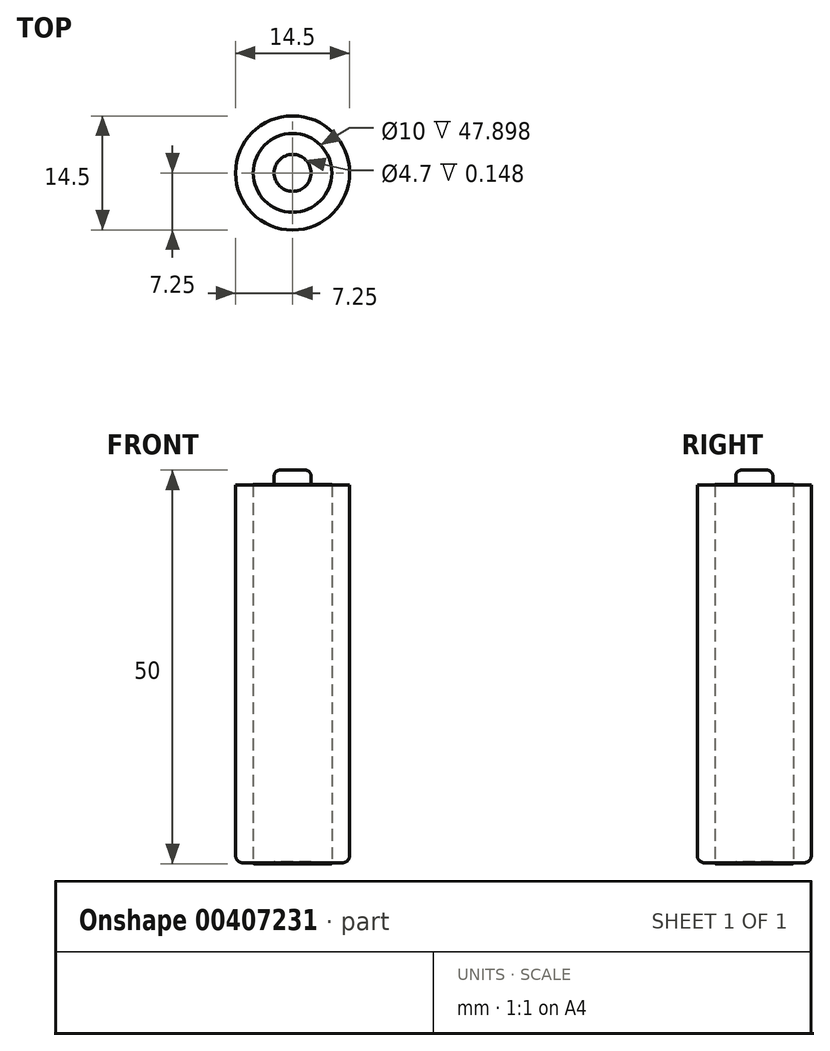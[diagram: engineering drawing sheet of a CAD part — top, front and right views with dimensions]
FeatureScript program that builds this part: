
annotation { "Feature Type Name" : "Feature", "Feature Type Description" : "" }
export const myFeature = defineFeature(function(context is Context, id is Id, definition is map)
    precondition{}
    {
        {
            var Q0;
            Q0=qCreatedBy(makeId("Top.planeOp"),FACE);
            var sketch = newSketch(context, id + "F0", { "sketchPlane" : qUnion([Q0])});
            skCircle(sketch, "E0", {"center": v(0, 0) * mm, "radius": 7.25 * mm});
            skCircle(sketch, "E1", {"center": v(0, 0) * mm, "radius": 2.35 * mm});
            skCircle(sketch, "E2", {"center": v(0, 0) * mm, "radius": 5 * mm});
            skSolve(sketch);
        }
        {
            var Q0;
            Q0=makeQuery(id+"F0.imprint","IMPRINT",FACE,{"disambiguationData":[TD([[makeQuery(id+"F0.imprint","IMPRINT",EDGE,{"derivedFrom":sQuery(id+"F0.wireOp",EDGE,"E1")}),1.0]])]});
            extrude(context, id + "F1", {"entities" : qUnion([Q0]), "depth" : 50 * mm, "offsetDistance" : 25.4 * mm, "hasSecondDirection" : true, "secondDirectionOppositeDirection" : false, "secondDirectionDepth" : 0.25 * mm});
        }
        {
            var Q0;
            Q0=makeQuery(id+"F0.imprint","IMPRINT",FACE,{"disambiguationData":[TD([[makeQuery(id+"F0.imprint","IMPRINT",EDGE,{"derivedFrom":sQuery(id+"F0.wireOp",EDGE,"E1")}),-1.0]])]});
            var Q1;
            Q1=makeQuery(id+"F1.opExtrude","CAP_FACE",FACE,{"disambiguationData":[OSD([sQuery(id+"F0.wireOp",EDGE,"E1")])],"isStart":false});
            extrude(context, id + "F2", {"entities" : qUnion([Q0]), "operationType" : NewBodyOperationType.ADD, "endBound" : BoundingType.UP_TO_SURFACE, "depth" : 25.4 * mm, "endBoundEntityFace" : qUnion([Q1]), "hasOffset" : true, "offsetDistance" : (50 - 48.2) * mm});
        }
        {
            var Q0;
            Q0=makeQuery(id+"F0.imprint","IMPRINT",FACE,{"disambiguationData":[TD([[makeQuery(id+"F0.imprint","IMPRINT",EDGE,{"derivedFrom":sQuery(id+"F0.wireOp",EDGE,"E0")}),1.0]])]});
            var Q1;
            Q1=makeQuery(id+"F2.opExtrude","CAP_FACE",FACE,{"disambiguationData":[OSD([sQuery(id+"F0.wireOp",EDGE,"E1")])],"isStart":false});
            extrude(context, id + "F3", {"entities" : qUnion([Q0]), "endBound" : BoundingType.UP_TO_SURFACE, "depth" : 25.4 * mm, "endBoundEntityFace" : qUnion([Q1]), "hasOffset" : true, "offsetDistance" : 0.1 * mm, "hasSecondDirection" : true, "secondDirectionOppositeDirection" : false, "secondDirectionDepth" : 0.1 * mm});
        }
        {
            var Q0;
            Q0=makeQuery(id+"F3.opExtrude","TWEAK_EDGE",EDGE,{"derivedFrom":[makeQuery(id+"F0.imprint","IMPRINT",EDGE,{"derivedFrom":sQuery(id+"F0.wireOp",EDGE,"E0")}),makeQuery(id+"F2.opExtrude","CAP_FACE",FACE,{"disambiguationData":[OSD([sQuery(id+"F0.wireOp",EDGE,"E1")])],"isStart":false})]});
            var Q1;
            Q1=makeQuery(id+"F3.opExtrude","CAP_EDGE",EDGE,{"disambiguationData":[OSD([sQuery(id+"F0.wireOp",EDGE,"E0")])],"isStart":true});
            fillet(context, id + "F4", {"entities" : qUnion([Q0, Q1]), "radius" : 0.95 * mm, "tangentPropagation" : true, "allowEdgeOverflow" : false});
        }
        {
            var Q0;
            Q0=makeQuery(id+"F2.opExtrude","TWEAK_EDGE",EDGE,{"derivedFrom":[makeQuery(id+"F0.imprint","IMPRINT",EDGE,{"derivedFrom":sQuery(id+"F0.wireOp",EDGE,"E2")}),makeQuery(id+"F1.opExtrude","CAP_FACE",FACE,{"disambiguationData":[OSD([sQuery(id+"F0.wireOp",EDGE,"E1")])],"isStart":false})]});
            var Q1;
            Q1=makeQuery(id+"F3.opExtrude","TWEAK_EDGE",EDGE,{"derivedFrom":[makeQuery(id+"F0.imprint","IMPRINT",EDGE,{"derivedFrom":sQuery(id+"F0.wireOp",EDGE,"E2")}),makeQuery(id+"F2.opExtrude","CAP_FACE",FACE,{"disambiguationData":[OSD([sQuery(id+"F0.wireOp",EDGE,"E1")])],"isStart":false})]});
            var Q2;
            Q2=makeQuery(id+"F3.opExtrude","CAP_EDGE",EDGE,{"disambiguationData":[OSD([sQuery(id+"F0.wireOp",EDGE,"E2")])],"isStart":true});
            var Q3;
            Q3=makeQuery(id+"F2.opExtrude","CAP_EDGE",EDGE,{"disambiguationData":[OSD([sQuery(id+"F0.wireOp",EDGE,"E2")])],"isStart":true});
            var Q4;
            Q4=makeQuery(id+"F2.opExtrude","CAP_EDGE",EDGE,{"disambiguationData":[OSD([sQuery(id+"F0.wireOp",EDGE,"E1")])],"isStart":true});
            var Q5;
            Q5=makeQuery(id+"F1.opExtrude","CAP_EDGE",EDGE,{"disambiguationData":[OSD([sQuery(id+"F0.wireOp",EDGE,"E1")])],"isStart":true});
            fillet(context, id + "F5", {"entities" : qUnion([Q0, Q1, Q2, Q3, Q4, Q5]), "radius" : 0.1 * mm, "tangentPropagation" : true, "allowEdgeOverflow" : false});
        }
        {
            var Q0;
            {var subQ0=sQuery(id+"F0.wireOp",EDGE,"E1");Q0=makeQuery(id+"F2.opExtrude","TWEAK_EDGE",EDGE,{"derivedFrom":[makeQuery(id+"F0.imprint","IMPRINT",EDGE,{"derivedFrom":subQ0}),makeQuery(id+"F1.opExtrude","CAP_FACE",FACE,{"disambiguationData":[OSD([subQ0])],"isStart":false})]});}
            var Q1;
            Q1=makeQuery(id+"F1.opExtrude","CAP_EDGE",EDGE,{"disambiguationData":[OSD([sQuery(id+"F0.wireOp",EDGE,"E1")])],"isStart":false});
            fillet(context, id + "F6", {"entities" : qUnion([Q0, Q1]), "radius" : 0.76 * mm, "tangentPropagation" : true, "allowEdgeOverflow" : false});
        }
    });
